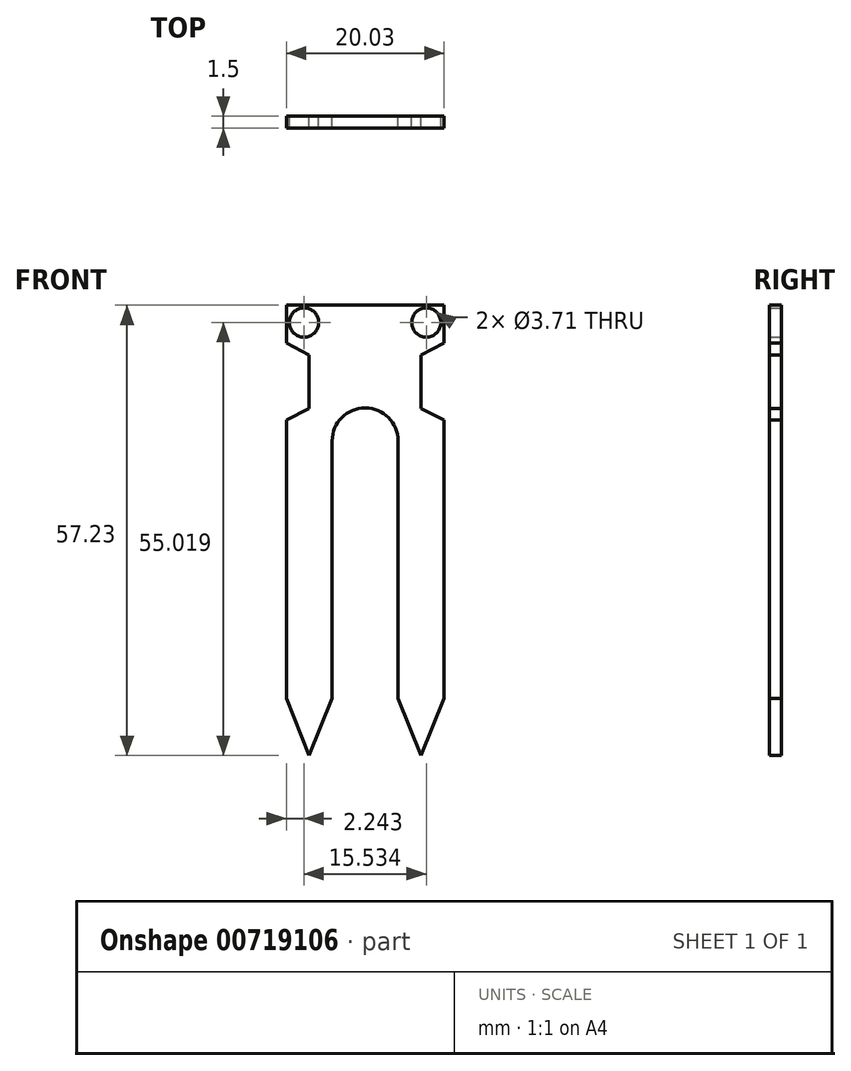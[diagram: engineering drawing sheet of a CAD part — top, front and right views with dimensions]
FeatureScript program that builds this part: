
annotation { "Feature Type Name" : "Feature", "Feature Type Description" : "" }
export const myFeature = defineFeature(function(context is Context, id is Id, definition is map)
    precondition{}
    {
        {
            var Q0;
            Q0=qCreatedBy(makeId("Front.planeOp"),FACE);
            var sketch = newSketch(context, id + "F0", { "sketchPlane" : qUnion([Q0])});
            skLineSegment(sketch, "E0", {"start": v(0, 6.33) * mm, "end": v(10.02, 6.33) * mm});
            skLineSegment(sketch, "E1", {"start": v(10.01, 6.33) * mm, "end": v(10.01, 1.49) * mm});
            skLineSegment(sketch, "E2", {"start": v(10.02, 1.49) * mm, "end": v(7.12, 0) * mm});
            skLineSegment(sketch, "E3", {"start": v(7.11, 0) * mm, "end": v(7.11, -6.78) * mm});
            skLineSegment(sketch, "E4", {"start": v(7.12, -6.78) * mm, "end": v(10.02, -8.27) * mm});
            skLineSegment(sketch, "E5", {"start": v(10.01, -8.27) * mm, "end": v(10.01, -43.6) * mm});
            skLineSegment(sketch, "E6", {"start": v(10.02, -43.6) * mm, "end": v(7.1, -50.9) * mm});
            skLineSegment(sketch, "E7", {"start": v(7.1, -50.9) * mm, "end": v(4.2, -43.6) * mm});
            skLineSegment(sketch, "E8", {"start": v(4.2, -43.6) * mm, "end": v(4.2, -10.9) * mm});
            skLineSegment(sketch, "E9", {"start": v(0, 13.62) * mm, "end": v(0, -50.05) * mm, "construction": true});
            skLineSegment(sketch, "E10", {"start": v(0, -50.05) * mm, "end": v(0, 8.65) * mm, "construction": true});
            skLineSegment(sketch, "E11.MirrorCS", {"start": v(0, 6.33) * mm, "end": v(-10.02, 6.33) * mm});
            skLineSegment(sketch, "E12.MirrorCS", {"start": v(-10.02, 6.33) * mm, "end": v(-10.02, 1.49) * mm});
            skLineSegment(sketch, "E13.MirrorCS", {"start": v(-10.01, 1.49) * mm, "end": v(-7.12, 0) * mm});
            skLineSegment(sketch, "E14.MirrorCS", {"start": v(-7.12, 0) * mm, "end": v(-7.12, -6.78) * mm});
            skLineSegment(sketch, "E15.MirrorCS", {"start": v(-7.12, -6.78) * mm, "end": v(-10.02, -8.27) * mm});
            skLineSegment(sketch, "E16.MirrorCS", {"start": v(-10.02, -8.27) * mm, "end": v(-10.02, -43.6) * mm});
            skLineSegment(sketch, "E17.MirrorCS", {"start": v(-10.01, -43.6) * mm, "end": v(-7.1, -50.9) * mm});
            skLineSegment(sketch, "E18.MirrorCS", {"start": v(-7.1, -50.9) * mm, "end": v(-4.2, -43.6) * mm});
            skLineSegment(sketch, "E19.MirrorCS", {"start": v(-4.2, -43.6) * mm, "end": v(-4.2, -10.9) * mm});
            skCircle(sketch, "E20", {"center": v(7.77, 4.12) * mm, "radius": 1.86 * mm});
            skCircle(sketch, "E21.MirrorC", {"center": v(-7.77, 4.12) * mm, "radius": 1.86 * mm});
            skCircle(sketch, "E22", {"center": v(-7.77, 4.12) * mm, "radius": 0.18 * mm, "construction": true});
            skArc(sketch, "E23", {"start": v(4.2, -10.9) * mm, "mid": v(0, -6.71) * mm, "end": v(-4.2, -10.9) * mm});
            skSolve(sketch);
        }
        {
            var Q0;
            Q0=makeQuery(id+"F0.imprint","IMPRINT",FACE,{"disambiguationData":[TD([[makeQuery(id+"F0.imprint","IMPRINT",EDGE,{"derivedFrom":sQuery(id+"F0.wireOp",EDGE,"E0")}),-1.0]])]});
            extrude(context, id + "F1", {"entities" : qUnion([Q0]), "depth" : 1.5 * mm, "offsetDistance" : 25 * mm});
        }
    });
